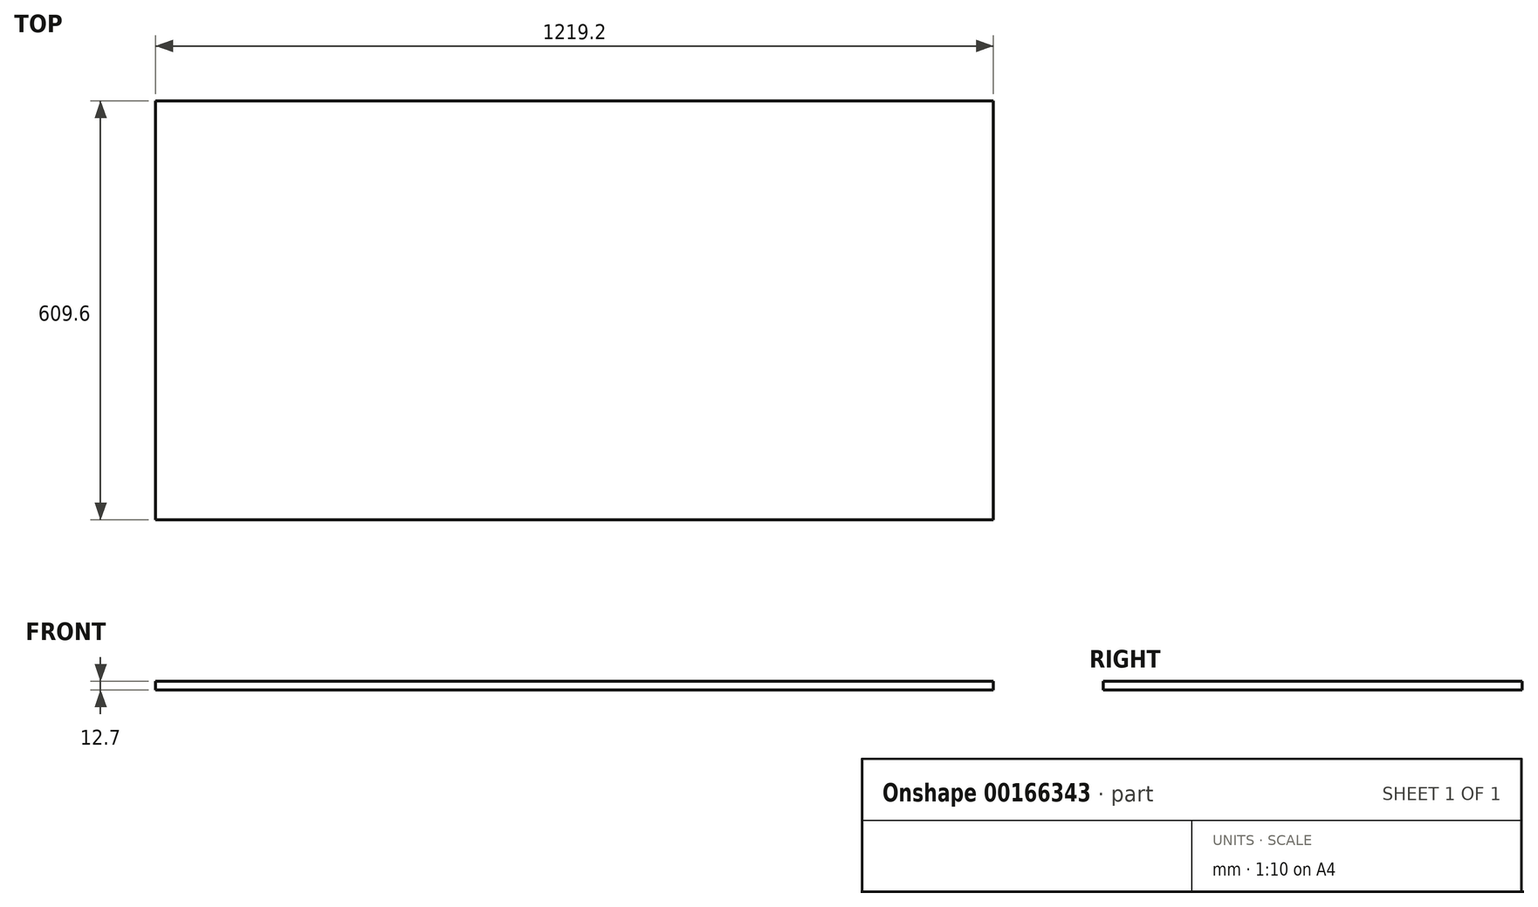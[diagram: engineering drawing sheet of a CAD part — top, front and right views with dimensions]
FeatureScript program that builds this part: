
annotation { "Feature Type Name" : "Feature", "Feature Type Description" : "" }
export const myFeature = defineFeature(function(context is Context, id is Id, definition is map)
    precondition{}
    {
        {
            var Q0;
            Q0=qCreatedBy(makeId("Top.planeOp"),FACE);
            var sketch = newSketch(context, id + "F0", { "sketchPlane" : qUnion([Q0])});
            skLineSegment(sketch, "E0.bottom", {"start": v(609.6, 304.8) * mm, "end": v(-609.6, 304.8) * mm});
            skLineSegment(sketch, "E0.top", {"start": v(609.6, -304.8) * mm, "end": v(-609.6, -304.8) * mm});
            skLineSegment(sketch, "E0.left", {"start": v(609.6, 304.8) * mm, "end": v(609.6, -304.8) * mm});
            skLineSegment(sketch, "E0.right", {"start": v(-609.6, 304.8) * mm, "end": v(-609.6, -304.8) * mm});
            skPoint(sketch, "E0.middle", {"position": v(0, 0) * mm});
            skSolve(sketch);
        }
        {
            var Q0;
            Q0 = qSketchRegion(id + "F0", true);
            extrude(context, id + "F1", {"entities" : qUnion([Q0]), "depth" : 12.7 * mm});
        }
    });
